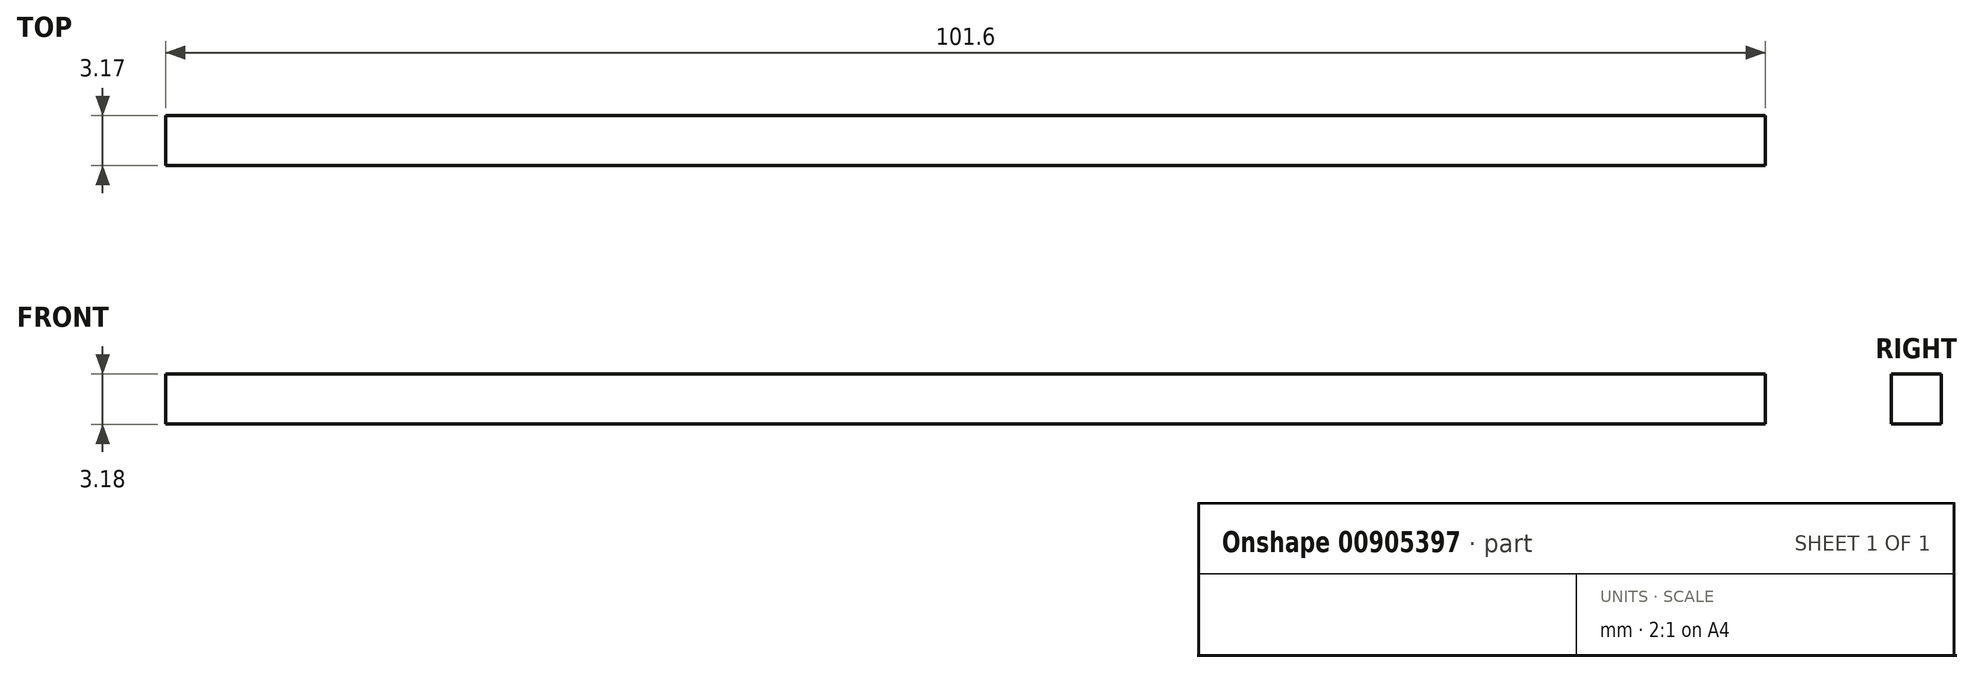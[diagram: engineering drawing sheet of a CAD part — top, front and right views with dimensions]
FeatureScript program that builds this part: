
annotation { "Feature Type Name" : "Feature", "Feature Type Description" : "" }
export const myFeature = defineFeature(function(context is Context, id is Id, definition is map)
    precondition{}
    {
        {
            var Q0;
            Q0=qCreatedBy(makeId("Front.planeOp"),FACE);
            var sketch = newSketch(context, id + "F0", { "sketchPlane" : qUnion([Q0])});
            skLineSegment(sketch, "E0.bottom", {"start": v(-50.8, 1.59) * mm, "end": v(50.8, 1.59) * mm});
            skLineSegment(sketch, "E0.top", {"start": v(-50.8, -1.59) * mm, "end": v(50.8, -1.59) * mm});
            skLineSegment(sketch, "E0.left", {"start": v(-50.8, 1.59) * mm, "end": v(-50.8, -1.59) * mm});
            skLineSegment(sketch, "E0.right", {"start": v(50.8, 1.59) * mm, "end": v(50.8, -1.59) * mm});
            skLineSegment(sketch, "E1", {"start": v(-50.8, 1.59) * mm, "end": v(50.8, -1.59) * mm, "construction": true});
            skSolve(sketch);
        }
        {
            var Q0;
            Q0 = qSketchRegion(id + "F0", true);
            extrude(context, id + "F1", {"entities" : qUnion([Q0]), "depth" : 3.17 * mm, "offsetDistance" : 25.4 * mm});
        }
    });
